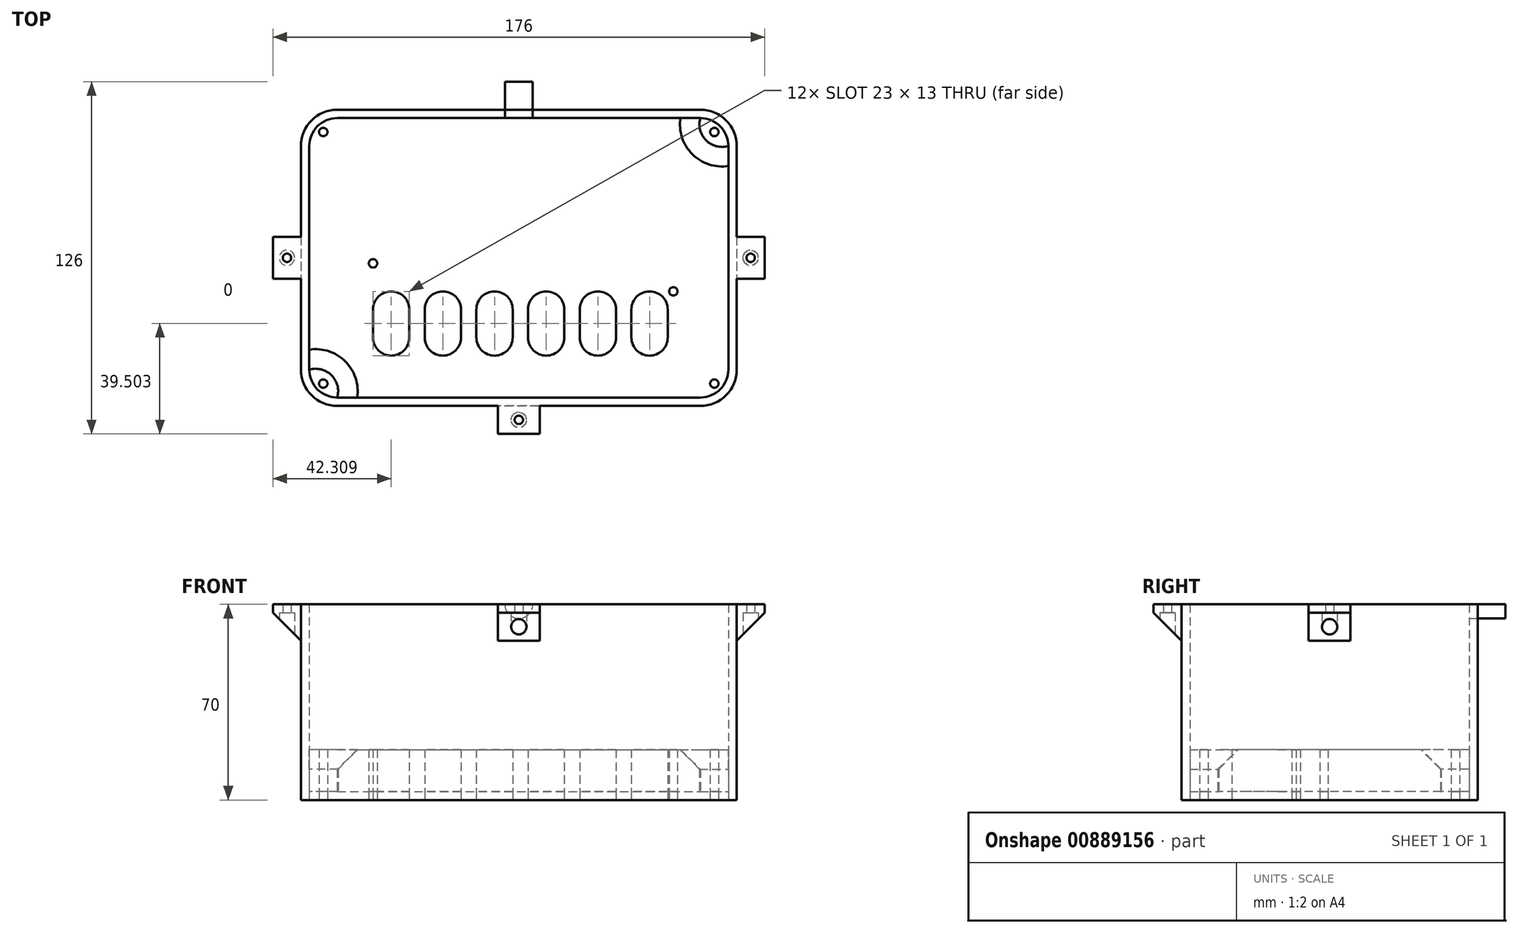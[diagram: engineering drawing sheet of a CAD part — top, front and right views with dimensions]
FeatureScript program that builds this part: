
annotation { "Feature Type Name" : "Feature", "Feature Type Description" : "" }
export const myFeature = defineFeature(function(context is Context, id is Id, definition is map)
    precondition{}
    {
        {
            var Q0;
            Q0=qCreatedBy(makeId("Top.planeOp"),FACE);
            var sketch = newSketch(context, id + "F0", { "sketchPlane" : qUnion([Q0])});
            skLineSegment(sketch, "E0.bottom", {"start": v(-27.14, 18.01) * mm, "end": v(-27.14, 18.01) * mm});
            skLineSegment(sketch, "E0.top", {"start": v(-27.14, -3.99) * mm, "end": v(-27.14, -3.99) * mm});
            skLineSegment(sketch, "E0.left", {"start": v(-33.14, 12.01) * mm, "end": v(-33.14, 2.01) * mm});
            skLineSegment(sketch, "E0.right", {"start": v(-21.14, 12.01) * mm, "end": v(-21.14, 2.01) * mm});
            skPoint(sketch, "E1.visualSharp", {"position": v(-33.14, 18.01) * mm});
            skArc(sketch, "E1.filletArc", {"start": v(-27.14, 18.01) * mm, "mid": v(-31.38, 16.26) * mm, "end": v(-33.14, 12.01) * mm});
            skPoint(sketch, "E2.visualSharp", {"position": v(-21.14, 18.01) * mm});
            skArc(sketch, "E2.filletArc", {"start": v(-21.14, 12.01) * mm, "mid": v(-22.9, 16.26) * mm, "end": v(-27.14, 18.01) * mm});
            skPoint(sketch, "E3.visualSharp", {"position": v(-33.14, -3.99) * mm});
            skArc(sketch, "E3.filletArc", {"start": v(-33.14, 2.01) * mm, "mid": v(-31.38, -2.23) * mm, "end": v(-27.14, -3.99) * mm});
            skArc(sketch, "E4.filletArc", {"start": v(-27.14, -3.99) * mm, "mid": v(-22.9, -2.23) * mm, "end": v(-21.14, 2.01) * mm});
            skArc(sketch, "E5.0", {"start": v(-20.64, 12.01) * mm, "mid": v(-22.49, 16.55) * mm, "end": v(-26.97, 18.51) * mm});
            skArc(sketch, "E5.1", {"start": v(-26.97, -4.49) * mm, "mid": v(-22.49, -2.52) * mm, "end": v(-20.64, 2.01) * mm});
            skArc(sketch, "E5.2", {"start": v(-33.64, 2.01) * mm, "mid": v(-31.68, -2.64) * mm, "end": v(-26.97, -4.49) * mm});
            skLineSegment(sketch, "E5.3", {"start": v(-20.64, 12.01) * mm, "end": v(-20.64, 2.01) * mm});
            skLineSegment(sketch, "E5.4", {"start": v(-33.64, 12.01) * mm, "end": v(-33.64, 2.01) * mm});
            skArc(sketch, "E5.5", {"start": v(-26.97, 18.51) * mm, "mid": v(-31.68, 16.67) * mm, "end": v(-33.64, 12.01) * mm});
            skArc(sketch, "E6.1.0.0", {"start": v(-8.64, 18.01) * mm, "mid": v(-12.88, 16.26) * mm, "end": v(-14.64, 12.01) * mm});
            skArc(sketch, "E6.1.0.1", {"start": v(-8.47, -4.49) * mm, "mid": v(-3.99, -2.52) * mm, "end": v(-2.14, 2.01) * mm});
            skArc(sketch, "E6.1.0.2", {"start": v(-2.14, 12.01) * mm, "mid": v(-3.99, 16.55) * mm, "end": v(-8.47, 18.51) * mm});
            skLineSegment(sketch, "E6.1.0.3", {"start": v(-2.14, 12.01) * mm, "end": v(-2.14, 2.01) * mm});
            skArc(sketch, "E6.1.0.4", {"start": v(-2.64, 12.01) * mm, "mid": v(-4.4, 16.26) * mm, "end": v(-8.64, 18.01) * mm});
            skArc(sketch, "E6.1.0.5", {"start": v(-14.64, 2.01) * mm, "mid": v(-12.88, -2.23) * mm, "end": v(-8.64, -3.99) * mm});
            skArc(sketch, "E6.1.0.6", {"start": v(-8.64, -3.99) * mm, "mid": v(-4.4, -2.23) * mm, "end": v(-2.64, 2.01) * mm});
            skPoint(sketch, "E6.1.0.7", {"position": v(-14.64, -3.99) * mm});
            skPoint(sketch, "E6.1.0.8", {"position": v(-2.64, 18.01) * mm});
            skLineSegment(sketch, "E6.1.0.9", {"start": v(-15.14, 12.01) * mm, "end": v(-15.14, 2.01) * mm});
            skLineSegment(sketch, "E6.1.0.10", {"start": v(-14.64, 12.01) * mm, "end": v(-14.64, 2.01) * mm});
            skArc(sketch, "E6.1.0.11", {"start": v(-8.47, 18.51) * mm, "mid": v(-13.18, 16.67) * mm, "end": v(-15.14, 12.01) * mm});
            skPoint(sketch, "E6.1.0.12", {"position": v(-14.64, 18.01) * mm});
            skLineSegment(sketch, "E6.1.0.13", {"start": v(-2.64, 12.01) * mm, "end": v(-2.64, 2.01) * mm});
            skArc(sketch, "E6.1.0.14", {"start": v(-15.14, 2.01) * mm, "mid": v(-13.18, -2.64) * mm, "end": v(-8.47, -4.49) * mm});
            skArc(sketch, "E6.2.0.0", {"start": v(9.86, 18.01) * mm, "mid": v(5.62, 16.26) * mm, "end": v(3.86, 12.01) * mm});
            skArc(sketch, "E6.2.0.1", {"start": v(10.03, -4.49) * mm, "mid": v(14.51, -2.52) * mm, "end": v(16.36, 2.01) * mm});
            skArc(sketch, "E6.2.0.2", {"start": v(16.36, 12.01) * mm, "mid": v(14.51, 16.55) * mm, "end": v(10.03, 18.51) * mm});
            skLineSegment(sketch, "E6.2.0.3", {"start": v(16.36, 12.01) * mm, "end": v(16.36, 2.01) * mm});
            skArc(sketch, "E6.2.0.4", {"start": v(15.86, 12.01) * mm, "mid": v(14.1, 16.26) * mm, "end": v(9.86, 18.01) * mm});
            skArc(sketch, "E6.2.0.5", {"start": v(3.86, 2.01) * mm, "mid": v(5.62, -2.23) * mm, "end": v(9.86, -3.99) * mm});
            skArc(sketch, "E6.2.0.6", {"start": v(9.86, -3.99) * mm, "mid": v(14.1, -2.23) * mm, "end": v(15.86, 2.01) * mm});
            skPoint(sketch, "E6.2.0.7", {"position": v(3.86, -3.99) * mm});
            skPoint(sketch, "E6.2.0.8", {"position": v(15.86, 18.01) * mm});
            skLineSegment(sketch, "E6.2.0.9", {"start": v(3.36, 12.01) * mm, "end": v(3.36, 2.01) * mm});
            skLineSegment(sketch, "E6.2.0.10", {"start": v(3.86, 12.01) * mm, "end": v(3.86, 2.01) * mm});
            skArc(sketch, "E6.2.0.11", {"start": v(10.03, 18.51) * mm, "mid": v(5.32, 16.67) * mm, "end": v(3.36, 12.01) * mm});
            skPoint(sketch, "E6.2.0.12", {"position": v(3.86, 18.01) * mm});
            skLineSegment(sketch, "E6.2.0.13", {"start": v(15.86, 12.01) * mm, "end": v(15.86, 2.01) * mm});
            skArc(sketch, "E6.2.0.14", {"start": v(3.36, 2.01) * mm, "mid": v(5.32, -2.64) * mm, "end": v(10.03, -4.49) * mm});
            skArc(sketch, "E6.3.0.0", {"start": v(28.36, 18.01) * mm, "mid": v(24.12, 16.26) * mm, "end": v(22.36, 12.01) * mm});
            skArc(sketch, "E6.3.0.1", {"start": v(28.53, -4.49) * mm, "mid": v(33.01, -2.52) * mm, "end": v(34.86, 2.01) * mm});
            skArc(sketch, "E6.3.0.2", {"start": v(34.86, 12.01) * mm, "mid": v(33.01, 16.55) * mm, "end": v(28.53, 18.51) * mm});
            skLineSegment(sketch, "E6.3.0.3", {"start": v(34.86, 12.01) * mm, "end": v(34.86, 2.01) * mm});
            skArc(sketch, "E6.3.0.4", {"start": v(34.36, 12.01) * mm, "mid": v(32.6, 16.26) * mm, "end": v(28.36, 18.01) * mm});
            skArc(sketch, "E6.3.0.5", {"start": v(22.36, 2.01) * mm, "mid": v(24.12, -2.23) * mm, "end": v(28.36, -3.99) * mm});
            skArc(sketch, "E6.3.0.6", {"start": v(28.36, -3.99) * mm, "mid": v(32.6, -2.23) * mm, "end": v(34.36, 2.01) * mm});
            skPoint(sketch, "E6.3.0.7", {"position": v(22.36, -3.99) * mm});
            skPoint(sketch, "E6.3.0.8", {"position": v(34.36, 18.01) * mm});
            skLineSegment(sketch, "E6.3.0.9", {"start": v(21.86, 12.01) * mm, "end": v(21.86, 2.01) * mm});
            skLineSegment(sketch, "E6.3.0.10", {"start": v(22.36, 12.01) * mm, "end": v(22.36, 2.01) * mm});
            skArc(sketch, "E6.3.0.11", {"start": v(28.53, 18.51) * mm, "mid": v(23.82, 16.67) * mm, "end": v(21.86, 12.01) * mm});
            skPoint(sketch, "E6.3.0.12", {"position": v(22.36, 18.01) * mm});
            skLineSegment(sketch, "E6.3.0.13", {"start": v(34.36, 12.01) * mm, "end": v(34.36, 2.01) * mm});
            skArc(sketch, "E6.3.0.14", {"start": v(21.86, 2.01) * mm, "mid": v(23.82, -2.64) * mm, "end": v(28.53, -4.49) * mm});
            skArc(sketch, "E6.4.0.0", {"start": v(46.86, 18.01) * mm, "mid": v(42.62, 16.26) * mm, "end": v(40.86, 12.01) * mm});
            skArc(sketch, "E6.4.0.1", {"start": v(47.03, -4.49) * mm, "mid": v(51.51, -2.52) * mm, "end": v(53.36, 2.01) * mm});
            skArc(sketch, "E6.4.0.2", {"start": v(53.36, 12.01) * mm, "mid": v(51.51, 16.55) * mm, "end": v(47.03, 18.51) * mm});
            skLineSegment(sketch, "E6.4.0.3", {"start": v(53.36, 12.01) * mm, "end": v(53.36, 2.01) * mm});
            skArc(sketch, "E6.4.0.4", {"start": v(52.86, 12.01) * mm, "mid": v(51.1, 16.26) * mm, "end": v(46.86, 18.01) * mm});
            skArc(sketch, "E6.4.0.5", {"start": v(40.86, 2.01) * mm, "mid": v(42.62, -2.23) * mm, "end": v(46.86, -3.99) * mm});
            skArc(sketch, "E6.4.0.6", {"start": v(46.86, -3.99) * mm, "mid": v(51.1, -2.23) * mm, "end": v(52.86, 2.01) * mm});
            skPoint(sketch, "E6.4.0.7", {"position": v(40.86, -3.99) * mm});
            skPoint(sketch, "E6.4.0.8", {"position": v(52.86, 18.01) * mm});
            skLineSegment(sketch, "E6.4.0.9", {"start": v(40.36, 12.01) * mm, "end": v(40.36, 2.01) * mm});
            skLineSegment(sketch, "E6.4.0.10", {"start": v(40.86, 12.01) * mm, "end": v(40.86, 2.01) * mm});
            skArc(sketch, "E6.4.0.11", {"start": v(47.03, 18.51) * mm, "mid": v(42.32, 16.67) * mm, "end": v(40.36, 12.01) * mm});
            skPoint(sketch, "E6.4.0.12", {"position": v(40.86, 18.01) * mm});
            skLineSegment(sketch, "E6.4.0.13", {"start": v(52.86, 12.01) * mm, "end": v(52.86, 2.01) * mm});
            skArc(sketch, "E6.4.0.14", {"start": v(40.36, 2.01) * mm, "mid": v(42.32, -2.64) * mm, "end": v(47.03, -4.49) * mm});
            skArc(sketch, "E6.5.0.0", {"start": v(65.36, 18.01) * mm, "mid": v(61.12, 16.26) * mm, "end": v(59.36, 12.01) * mm});
            skArc(sketch, "E6.5.0.1", {"start": v(65.53, -4.49) * mm, "mid": v(70.01, -2.52) * mm, "end": v(71.86, 2.01) * mm});
            skArc(sketch, "E6.5.0.2", {"start": v(71.86, 12.01) * mm, "mid": v(70.01, 16.55) * mm, "end": v(65.53, 18.51) * mm});
            skLineSegment(sketch, "E6.5.0.3", {"start": v(71.86, 12.01) * mm, "end": v(71.86, 2.01) * mm});
            skArc(sketch, "E6.5.0.4", {"start": v(71.36, 12.01) * mm, "mid": v(69.6, 16.26) * mm, "end": v(65.36, 18.01) * mm});
            skArc(sketch, "E6.5.0.5", {"start": v(59.36, 2.01) * mm, "mid": v(61.12, -2.23) * mm, "end": v(65.36, -3.99) * mm});
            skArc(sketch, "E6.5.0.6", {"start": v(65.36, -3.99) * mm, "mid": v(69.6, -2.23) * mm, "end": v(71.36, 2.01) * mm});
            skPoint(sketch, "E6.5.0.7", {"position": v(59.36, -3.99) * mm});
            skPoint(sketch, "E6.5.0.8", {"position": v(71.36, 18.01) * mm});
            skLineSegment(sketch, "E6.5.0.9", {"start": v(58.86, 12.01) * mm, "end": v(58.86, 2.01) * mm});
            skLineSegment(sketch, "E6.5.0.10", {"start": v(59.36, 12.01) * mm, "end": v(59.36, 2.01) * mm});
            skArc(sketch, "E6.5.0.11", {"start": v(65.53, 18.51) * mm, "mid": v(60.82, 16.67) * mm, "end": v(58.86, 12.01) * mm});
            skPoint(sketch, "E6.5.0.12", {"position": v(59.36, 18.01) * mm});
            skLineSegment(sketch, "E6.5.0.13", {"start": v(71.36, 12.01) * mm, "end": v(71.36, 2.01) * mm});
            skArc(sketch, "E6.5.0.14", {"start": v(58.86, 2.01) * mm, "mid": v(60.82, -2.64) * mm, "end": v(65.53, -4.49) * mm});
            skLineSegment(sketch, "E6.direction1", {"start": v(-33.14, -3.99) * mm, "end": v(-14.64, -3.99) * mm, "construction": true});
            skLineSegment(sketch, "E7", {"start": v(-21.14, 12.01) * mm, "end": v(-14.64, 12.01) * mm});
            skPoint(sketch, "E8", {"position": v(71.86, 18.51) * mm});
            skLineSegment(sketch, "E9", {"start": v(-8.47, 18.51) * mm, "end": v(-37.8, 18.51) * mm, "construction": true});
            skLineSegment(sketch, "E10.trimOffspring", {"start": v(-33.64, 18.51) * mm, "end": v(-33.64, 28.51) * mm, "construction": true});
            skLineSegment(sketch, "E11.bottom", {"start": v(-46.45, 80.51) * mm, "end": v(83.55, 80.51) * mm});
            skLineSegment(sketch, "E11.top", {"start": v(-46.45, -19.49) * mm, "end": v(83.55, -19.49) * mm});
            skLineSegment(sketch, "E11.left", {"start": v(-56.45, 70.51) * mm, "end": v(-56.45, -9.49) * mm});
            skLineSegment(sketch, "E11.right", {"start": v(93.55, 70.51) * mm, "end": v(93.55, -9.49) * mm});
            skLineSegment(sketch, "E12", {"start": v(-56.45, 80.51) * mm, "end": v(93.55, -19.49) * mm, "construction": true});
            skLineSegment(sketch, "E13", {"start": v(93.55, 80.51) * mm, "end": v(-56.45, -19.49) * mm, "construction": true});
            skLineSegment(sketch, "E14", {"start": v(18.55, -19.49) * mm, "end": v(18.55, 80.51) * mm, "construction": true});
            skLineSegment(sketch, "E15", {"start": v(10.03, -4.49) * mm, "end": v(10.03, -19.49) * mm, "construction": true});
            skPoint(sketch, "E16.visualSharp", {"position": v(93.55, 80.51) * mm});
            skArc(sketch, "E16.filletArc", {"start": v(93.55, 70.51) * mm, "mid": v(90.62, 77.59) * mm, "end": v(83.55, 80.51) * mm});
            skPoint(sketch, "E17.visualSharp", {"position": v(-56.45, 80.51) * mm});
            skArc(sketch, "E17.filletArc", {"start": v(-46.45, 80.51) * mm, "mid": v(-53.52, 77.59) * mm, "end": v(-56.45, 70.51) * mm});
            skPoint(sketch, "E18.visualSharp", {"position": v(-56.45, -19.49) * mm});
            skArc(sketch, "E18.filletArc", {"start": v(-56.45, -9.49) * mm, "mid": v(-53.52, -16.56) * mm, "end": v(-46.45, -19.49) * mm});
            skPoint(sketch, "E19.visualSharp", {"position": v(93.55, -19.49) * mm});
            skArc(sketch, "E19.filletArc", {"start": v(83.55, -19.49) * mm, "mid": v(90.62, -16.56) * mm, "end": v(93.55, -9.49) * mm});
            skArc(sketch, "E20.0", {"start": v(-59.45, -9.49) * mm, "mid": v(-55.64, -18.68) * mm, "end": v(-46.45, -22.49) * mm});
            skLineSegment(sketch, "E20.1", {"start": v(-59.45, 70.51) * mm, "end": v(-59.45, -9.49) * mm});
            skLineSegment(sketch, "E20.2", {"start": v(-46.45, -22.49) * mm, "end": v(83.55, -22.49) * mm});
            skArc(sketch, "E20.3", {"start": v(-46.45, 83.51) * mm, "mid": v(-55.64, 79.7) * mm, "end": v(-59.45, 70.51) * mm});
            skArc(sketch, "E20.4", {"start": v(83.55, -22.49) * mm, "mid": v(92.74, -18.68) * mm, "end": v(96.55, -9.49) * mm});
            skLineSegment(sketch, "E20.5", {"start": v(96.55, 70.51) * mm, "end": v(96.55, -9.49) * mm});
            skArc(sketch, "E20.6", {"start": v(96.55, 70.51) * mm, "mid": v(92.74, 79.7) * mm, "end": v(83.55, 83.51) * mm});
            skLineSegment(sketch, "E20.7", {"start": v(-46.45, 83.51) * mm, "end": v(83.55, 83.51) * mm});
            skLineSegment(sketch, "E21", {"start": v(71.86, 2.01) * mm, "end": v(71.86, 18.51) * mm, "construction": true});
            skLineSegment(sketch, "E22", {"start": v(28.53, 18.51) * mm, "end": v(65.53, 18.51) * mm, "construction": true});
            skLineSegment(sketch, "E23.trimOffspring", {"start": v(71.86, 18.51) * mm, "end": v(73.86, 18.51) * mm, "construction": true});
            skPoint(sketch, "E24", {"position": v(-33.64, 28.51) * mm});
            skLineSegment(sketch, "E25", {"start": v(93.55, -9.49) * mm, "end": v(83.55, -19.49) * mm, "construction": true});
            skPoint(sketch, "E26", {"position": v(88.55, -14.49) * mm});
            skLineSegment(sketch, "E27", {"start": v(-46.45, -19.49) * mm, "end": v(-56.45, -9.49) * mm, "construction": true});
            skLineSegment(sketch, "E28", {"start": v(-56.45, 70.51) * mm, "end": v(-46.45, 80.51) * mm, "construction": true});
            skLineSegment(sketch, "E29", {"start": v(93.55, 70.51) * mm, "end": v(83.55, 80.51) * mm, "construction": true});
            skPoint(sketch, "E30", {"position": v(-51.45, -14.49) * mm});
            skPoint(sketch, "E31", {"position": v(-51.45, 75.51) * mm});
            skPoint(sketch, "E32", {"position": v(88.55, 75.51) * mm});
            skSolve(sketch);
        }
        {
            var Q0;
            Q0=makeQuery(id+"F0.imprint","IMPRINT",FACE,{"disambiguationData":[TD([[makeQuery(id+"F0.imprint","IMPRINT",EDGE,{"derivedFrom":sQuery(id+"F0.wireOp",EDGE,"E5.0")}),-1.0]])]});
            extrude(context, id + "F1", {"entities" : qUnion([Q0]), "depth" : 3 * mm, "offsetDistance" : 25 * mm});
        }
        {
            var Q0;
            Q0=makeQuery(id+"F0.imprint","IMPRINT",FACE,{"disambiguationData":[TD([[makeQuery(id+"F0.imprint","IMPRINT",EDGE,{"derivedFrom":sQuery(id+"F0.wireOp",EDGE,"E11.bottom")}),1.0]])]});
            extrude(context, id + "F2", {"entities" : qUnion([Q0]), "depth" : 70 * mm, "offsetDistance" : 25 * mm});
        }
        {
            var Q0;
            Q0=makeQuery(id+"F2.opExtrude","SWEPT_FACE",FACE,{"disambiguationData":[OSD([sQuery(id+"F0.wireOp",EDGE,"E20.7")])]});
            var sketch = newSketch(context, id + "F3", { "sketchPlane" : qUnion([Q0])});
            skLineSegment(sketch, "E33", {"start": v(-83.55, 70) * mm, "end": v(46.45, 70) * mm, "construction": true});
            skPoint(sketch, "E34", {"position": v(-18.55, 70) * mm});
            skArc(sketch, "E35", {"start": v(-13.55, 70) * mm, "mid": v(-18.55, 65) * mm, "end": v(-23.55, 70) * mm});
            skArc(sketch, "E36.0", {"start": v(-11.55, 70) * mm, "mid": v(-18.55, 63) * mm, "end": v(-25.55, 70) * mm});
            skSolve(sketch);
        }
        {
            var Q0;
            Q0=sQuery(id+"F3.wireOp",VERTEX,"E34");
            var Q1;
            Q1=makeQuery(id+"F2.opExtrude","SWEPT_BODY",BODY,{"disambiguationData":[OSD([sQuery(id+"F0.wireOp",EDGE,"E11.bottom"),sQuery(id+"F0.wireOp",EDGE,"E11.top"),sQuery(id+"F0.wireOp",EDGE,"E11.left"),sQuery(id+"F0.wireOp",EDGE,"E11.right"),sQuery(id+"F0.wireOp",EDGE,"E16.filletArc"),sQuery(id+"F0.wireOp",EDGE,"E17.filletArc"),sQuery(id+"F0.wireOp",EDGE,"E18.filletArc"),sQuery(id+"F0.wireOp",EDGE,"E19.filletArc"),sQuery(id+"F0.wireOp",EDGE,"E20.0"),sQuery(id+"F0.wireOp",EDGE,"E20.1"),sQuery(id+"F0.wireOp",EDGE,"E20.2"),sQuery(id+"F0.wireOp",EDGE,"E20.3"),sQuery(id+"F0.wireOp",EDGE,"E20.4"),sQuery(id+"F0.wireOp",EDGE,"E20.5"),sQuery(id+"F0.wireOp",EDGE,"E20.6"),sQuery(id+"F0.wireOp",EDGE,"E20.7")])]});
            hole(context, id + "F4", {"style" : HoleStyle.SIMPLE, "endStyle" : HoleEndStyle.BLIND, "holeDiameter" : 10 * mm, "majorDiameter" : 5 * mm, "holeDepth" : 5 * mm, "isTappedThrough" : true, "tappedDepth" : 12 * mm, "tapClearance" : 3, "locations" : qUnion([Q0]), "scope" : qUnion([Q1])});
        }
        {
            var Q0;
            {var subQ0=sQuery(id+"F3.wireOp",EDGE,"E35");Q0=makeQuery(id+"F3.imprint","IMPRINT",FACE,{"disambiguationData":[TD([[makeQuery(id+"F3.imprint","IMPRINT",EDGE,{"derivedFrom":subQ0}),1.0]])]});}
            extrude(context, id + "F5", {"entities" : qUnion([Q0]), "operationType" : NewBodyOperationType.ADD, "depth" : 10 * mm, "offsetDistance" : 25 * mm});
        }
        {
            var Q0;
            {var subQ0=sQuery(id+"F3.wireOp",EDGE,"E35");var subQ1=sQuery(id+"F0.wireOp",EDGE,"E20.7");var subQ2=makeQuery(id+"F2.opExtrude","CAP_EDGE",EDGE,{"disambiguationData":[OSD([subQ1])],"isStart":false});Q0=makeQuery(id+"F5.boolean.opBoolean","MERGE",FACE,{"derivedFrom":[makeQuery(id+"F2.opExtrude","CAP_FACE",FACE,{"disambiguationData":[OSD([sQuery(id+"F0.wireOp",EDGE,"E11.bottom"),sQuery(id+"F0.wireOp",EDGE,"E11.top"),sQuery(id+"F0.wireOp",EDGE,"E11.left"),sQuery(id+"F0.wireOp",EDGE,"E11.right"),sQuery(id+"F0.wireOp",EDGE,"E16.filletArc"),sQuery(id+"F0.wireOp",EDGE,"E17.filletArc"),sQuery(id+"F0.wireOp",EDGE,"E18.filletArc"),sQuery(id+"F0.wireOp",EDGE,"E19.filletArc"),sQuery(id+"F0.wireOp",EDGE,"E20.0"),sQuery(id+"F0.wireOp",EDGE,"E20.1"),sQuery(id+"F0.wireOp",EDGE,"E20.2"),sQuery(id+"F0.wireOp",EDGE,"E20.3"),sQuery(id+"F0.wireOp",EDGE,"E20.4"),sQuery(id+"F0.wireOp",EDGE,"E20.5"),sQuery(id+"F0.wireOp",EDGE,"E20.6"),subQ1])],"isStart":false}),makeQuery(id+"F5.opExtrude","SWEPT_FACE",FACE,{"disambiguationData":[OSD([subQ1]),TDD([makeQuery(id+"F3.imprint","IMPRINT",EDGE,{"disambiguationData":[TD([[makeQuery(id+"F3.imprint","INTERSECT",VERTEX,{"disambiguationData":[OD(0.0)],"derivedFrom":[subQ2,subQ0]}),1.0]])],"derivedFrom":subQ2})])]}),makeQuery(id+"F5.opExtrude","SWEPT_FACE",FACE,{"disambiguationData":[OSD([subQ1]),TDD([makeQuery(id+"F3.imprint","IMPRINT",EDGE,{"disambiguationData":[TD([[makeQuery(id+"F3.imprint","INTERSECT",VERTEX,{"disambiguationData":[OD(1.0)],"derivedFrom":[subQ2,subQ0]}),-1.0]])],"derivedFrom":subQ2})])]})]});}
            var sketch = newSketch(context, id + "F6", { "sketchPlane" : qUnion([Q0])});
            skPoint(sketch, "E37.middle", {"position": v(-59.45, 30.51) * mm});
            skLineSegment(sketch, "E38.bottom", {"start": v(-59.45, 23.01) * mm, "end": v(-69.45, 23.01) * mm});
            skLineSegment(sketch, "E38.top", {"start": v(-59.45, 38.01) * mm, "end": v(-69.45, 38.01) * mm});
            skLineSegment(sketch, "E38.left", {"start": v(-59.45, 23.01) * mm, "end": v(-59.45, 38.01) * mm});
            skLineSegment(sketch, "E38.right", {"start": v(-69.45, 23.01) * mm, "end": v(-69.45, 38.01) * mm});
            skLineSegment(sketch, "E39", {"start": v(18.55, -22.49) * mm, "end": v(18.55, 80.54) * mm, "construction": true});
            skPoint(sketch, "E40.MirrorP", {"position": v(96.55, 30.51) * mm});
            skLineSegment(sketch, "E41.MirrorCS", {"start": v(96.55, 38.01) * mm, "end": v(106.55, 38.01) * mm});
            skLineSegment(sketch, "E42.MirrorCS", {"start": v(106.55, 23.01) * mm, "end": v(106.55, 38.01) * mm});
            skLineSegment(sketch, "E43.MirrorCS", {"start": v(96.55, 23.01) * mm, "end": v(106.55, 23.01) * mm});
            skLineSegment(sketch, "E44.MirrorCS", {"start": v(96.55, 23.01) * mm, "end": v(96.55, 38.01) * mm});
            skPoint(sketch, "E45.MirrorP", {"position": v(101.55, 30.51) * mm});
            skLineSegment(sketch, "E46.bottom", {"start": v(11.05, -22.49) * mm, "end": v(26.05, -22.49) * mm});
            skLineSegment(sketch, "E46.top", {"start": v(11.05, -32.49) * mm, "end": v(26.05, -32.49) * mm});
            skLineSegment(sketch, "E46.left", {"start": v(11.05, -22.49) * mm, "end": v(11.05, -32.49) * mm});
            skLineSegment(sketch, "E46.right", {"start": v(26.05, -22.49) * mm, "end": v(26.05, -32.49) * mm});
            skLineSegment(sketch, "E47", {"start": v(11.05, -22.49) * mm, "end": v(26.05, -32.49) * mm, "construction": true});
            skLineSegment(sketch, "E48", {"start": v(26.05, -22.49) * mm, "end": v(11.05, -32.49) * mm, "construction": true});
            skPoint(sketch, "E49", {"position": v(18.55, -27.49) * mm});
            skSolve(sketch);
        }
        {
            var Q0;
            Q0=makeQuery(id+"F6.imprint","IMPRINT",FACE,{"disambiguationData":[TD([[makeQuery(id+"F6.imprint","IMPRINT",EDGE,{"derivedFrom":sQuery(id+"F6.wireOp",EDGE,"E38.bottom")}),-1.0]])]});
            var Q1;
            Q1=makeQuery(id+"F6.imprint","IMPRINT",FACE,{"disambiguationData":[TD([[makeQuery(id+"F6.imprint","IMPRINT",EDGE,{"derivedFrom":sQuery(id+"F6.wireOp",EDGE,"E41.MirrorCS")}),-1.0]])]});
            var Q2;
            Q2=makeQuery(id+"F6.imprint","IMPRINT",FACE,{"disambiguationData":[TD([[makeQuery(id+"F6.imprint","IMPRINT",EDGE,{"derivedFrom":sQuery(id+"F6.wireOp",EDGE,"E46.bottom")}),-1.0]])]});
            extrude(context, id + "F7", {"entities" : qUnion([Q0, Q1, Q2]), "operationType" : NewBodyOperationType.ADD, "depth" : -15 * mm, "offsetDistance" : 25 * mm});
        }
        {
            var Q0;
            Q0=makeQuery(id+"F7.opExtrude","CAP_FACE",FACE,{"disambiguationData":[OSD([sQuery(id+"F6.wireOp",EDGE,"E38.bottom"),sQuery(id+"F6.wireOp",EDGE,"E38.top"),sQuery(id+"F6.wireOp",EDGE,"E38.left"),sQuery(id+"F6.wireOp",EDGE,"E38.right")])],"isStart":false});
            var sketch = newSketch(context, id + "F8", { "sketchPlane" : qUnion([Q0])});
            skLineSegment(sketch, "E50", {"start": v(-69.45, -23.01) * mm, "end": v(-59.45, -38.01) * mm, "construction": true});
            skLineSegment(sketch, "E51", {"start": v(-69.45, -38.01) * mm, "end": v(-59.45, -23.01) * mm, "construction": true});
            skPoint(sketch, "E52", {"position": v(-64.45, -30.51) * mm});
            skLineSegment(sketch, "E53", {"start": v(-59.45, -23.01) * mm, "end": v(96.55, -23.01) * mm, "construction": true});
            skLineSegment(sketch, "E54", {"start": v(18.55, -23.01) * mm, "end": v(18.55, 11.18) * mm});
            skPoint(sketch, "E55.MirrorP", {"position": v(101.55, -30.51) * mm});
            skSolve(sketch);
        }
        {
            var Q0;
            Q0=sQuery(id+"F8.wireOp",VERTEX,"E55.MirrorP");
            var Q1;
            Q1=sQuery(id+"F8.wireOp",VERTEX,"E52");
            var Q2;
            Q2=makeQuery(id+"F2.opExtrude","SWEPT_BODY",BODY,{"disambiguationData":[OSD([sQuery(id+"F0.wireOp",EDGE,"E11.bottom"),sQuery(id+"F0.wireOp",EDGE,"E11.top"),sQuery(id+"F0.wireOp",EDGE,"E11.left"),sQuery(id+"F0.wireOp",EDGE,"E11.right"),sQuery(id+"F0.wireOp",EDGE,"E16.filletArc"),sQuery(id+"F0.wireOp",EDGE,"E17.filletArc"),sQuery(id+"F0.wireOp",EDGE,"E18.filletArc"),sQuery(id+"F0.wireOp",EDGE,"E19.filletArc"),sQuery(id+"F0.wireOp",EDGE,"E20.0"),sQuery(id+"F0.wireOp",EDGE,"E20.1"),sQuery(id+"F0.wireOp",EDGE,"E20.2"),sQuery(id+"F0.wireOp",EDGE,"E20.3"),sQuery(id+"F0.wireOp",EDGE,"E20.4"),sQuery(id+"F0.wireOp",EDGE,"E20.5"),sQuery(id+"F0.wireOp",EDGE,"E20.6"),sQuery(id+"F0.wireOp",EDGE,"E20.7")])]});
            hole(context, id + "F9", {"style" : HoleStyle.C_BORE, "endStyle" : HoleEndStyle.BLIND, "holeDiameter" : 3 * mm, "cBoreDiameter" : 5.5 * mm, "cBoreDepth" : 12 * mm, "majorDiameter" : 5 * mm, "holeDepth" : 15 * mm, "isTappedThrough" : true, "tappedDepth" : 12 * mm, "tapClearance" : 3, "locations" : qUnion([Q0, Q1]), "scope" : qUnion([Q2])});
        }
        {
            var Q0;
            Q0=makeQuery(id+"F7.opExtrude","CAP_EDGE",EDGE,{"disambiguationData":[OSD([sQuery(id+"F6.wireOp",EDGE,"E38.right")])],"isStart":false});
            var Q1;
            Q1=makeQuery(id+"F7.opExtrude","CAP_EDGE",EDGE,{"disambiguationData":[OSD([sQuery(id+"F6.wireOp",EDGE,"E42.MirrorCS")])],"isStart":false});
            chamfer(context, id + "F10", {"entities" : qUnion([Q0, Q1]), "width" : 12 * mm, "tangentPropagation" : true});
        }
        {
            var Q0;
            Q0=sQuery(id+"F0.wireOp",VERTEX,"E24");
            var Q1;
            Q1=sQuery(id+"F0.wireOp",VERTEX,"E23.trimOffspring.end");
            var Q2;
            Q2=makeQuery(id+"F1.opExtrude","SWEPT_BODY",BODY,{"disambiguationData":[OSD([sQuery(id+"F0.wireOp",EDGE,"E5.0"),sQuery(id+"F0.wireOp",EDGE,"E5.1"),sQuery(id+"F0.wireOp",EDGE,"E5.2"),sQuery(id+"F0.wireOp",EDGE,"E5.3"),sQuery(id+"F0.wireOp",EDGE,"E5.4"),sQuery(id+"F0.wireOp",EDGE,"E5.5"),sQuery(id+"F0.wireOp",EDGE,"E6.1.0.1"),sQuery(id+"F0.wireOp",EDGE,"E6.1.0.2"),sQuery(id+"F0.wireOp",EDGE,"E6.1.0.3"),sQuery(id+"F0.wireOp",EDGE,"E6.1.0.9"),sQuery(id+"F0.wireOp",EDGE,"E6.1.0.11"),sQuery(id+"F0.wireOp",EDGE,"E6.1.0.14"),sQuery(id+"F0.wireOp",EDGE,"E6.2.0.1"),sQuery(id+"F0.wireOp",EDGE,"E6.2.0.2"),sQuery(id+"F0.wireOp",EDGE,"E6.2.0.3"),sQuery(id+"F0.wireOp",EDGE,"E6.2.0.9"),sQuery(id+"F0.wireOp",EDGE,"E6.2.0.11"),sQuery(id+"F0.wireOp",EDGE,"E6.2.0.14"),sQuery(id+"F0.wireOp",EDGE,"E6.3.0.1"),sQuery(id+"F0.wireOp",EDGE,"E6.3.0.2"),sQuery(id+"F0.wireOp",EDGE,"E6.3.0.3"),sQuery(id+"F0.wireOp",EDGE,"E6.3.0.9"),sQuery(id+"F0.wireOp",EDGE,"E6.3.0.11"),sQuery(id+"F0.wireOp",EDGE,"E6.3.0.14"),sQuery(id+"F0.wireOp",EDGE,"E6.4.0.1"),sQuery(id+"F0.wireOp",EDGE,"E6.4.0.2"),sQuery(id+"F0.wireOp",EDGE,"E6.4.0.3"),sQuery(id+"F0.wireOp",EDGE,"E6.4.0.9"),sQuery(id+"F0.wireOp",EDGE,"E6.4.0.11"),sQuery(id+"F0.wireOp",EDGE,"E6.4.0.14"),sQuery(id+"F0.wireOp",EDGE,"E6.5.0.1"),sQuery(id+"F0.wireOp",EDGE,"E6.5.0.2"),sQuery(id+"F0.wireOp",EDGE,"E6.5.0.3"),sQuery(id+"F0.wireOp",EDGE,"E6.5.0.9"),sQuery(id+"F0.wireOp",EDGE,"E6.5.0.11"),sQuery(id+"F0.wireOp",EDGE,"E6.5.0.14"),sQuery(id+"F0.wireOp",EDGE,"E11.bottom"),sQuery(id+"F0.wireOp",EDGE,"E11.top"),sQuery(id+"F0.wireOp",EDGE,"E11.left"),sQuery(id+"F0.wireOp",EDGE,"E11.right"),sQuery(id+"F0.wireOp",EDGE,"E16.filletArc"),sQuery(id+"F0.wireOp",EDGE,"E17.filletArc"),sQuery(id+"F0.wireOp",EDGE,"E18.filletArc"),sQuery(id+"F0.wireOp",EDGE,"E19.filletArc")])]});
            hole(context, id + "F11", {"style" : HoleStyle.SIMPLE, "endStyle" : HoleEndStyle.BLIND, "oppositeDirection" : true, "holeDiameter" : 3 * mm, "majorDiameter" : 5 * mm, "holeDepth" : 5 * mm, "isTappedThrough" : true, "tappedDepth" : 12 * mm, "tapClearance" : 3, "locations" : qUnion([Q0, Q1]), "scope" : qUnion([Q2])});
        }
        {
            var Q0;
            Q0=sQuery(id+"F0.wireOp",VERTEX,"E32");
            var Q1;
            Q1=sQuery(id+"F0.wireOp",VERTEX,"E31");
            var Q2;
            Q2=sQuery(id+"F0.wireOp",VERTEX,"E30");
            var Q3;
            Q3=sQuery(id+"F0.wireOp",VERTEX,"E26");
            var Q4;
            Q4=makeQuery(id+"F1.opExtrude","SWEPT_BODY",BODY,{"disambiguationData":[OSD([sQuery(id+"F0.wireOp",EDGE,"E5.0"),sQuery(id+"F0.wireOp",EDGE,"E5.1"),sQuery(id+"F0.wireOp",EDGE,"E5.2"),sQuery(id+"F0.wireOp",EDGE,"E5.3"),sQuery(id+"F0.wireOp",EDGE,"E5.4"),sQuery(id+"F0.wireOp",EDGE,"E5.5"),sQuery(id+"F0.wireOp",EDGE,"E6.1.0.1"),sQuery(id+"F0.wireOp",EDGE,"E6.1.0.2"),sQuery(id+"F0.wireOp",EDGE,"E6.1.0.3"),sQuery(id+"F0.wireOp",EDGE,"E6.1.0.9"),sQuery(id+"F0.wireOp",EDGE,"E6.1.0.11"),sQuery(id+"F0.wireOp",EDGE,"E6.1.0.14"),sQuery(id+"F0.wireOp",EDGE,"E6.2.0.1"),sQuery(id+"F0.wireOp",EDGE,"E6.2.0.2"),sQuery(id+"F0.wireOp",EDGE,"E6.2.0.3"),sQuery(id+"F0.wireOp",EDGE,"E6.2.0.9"),sQuery(id+"F0.wireOp",EDGE,"E6.2.0.11"),sQuery(id+"F0.wireOp",EDGE,"E6.2.0.14"),sQuery(id+"F0.wireOp",EDGE,"E6.3.0.1"),sQuery(id+"F0.wireOp",EDGE,"E6.3.0.2"),sQuery(id+"F0.wireOp",EDGE,"E6.3.0.3"),sQuery(id+"F0.wireOp",EDGE,"E6.3.0.9"),sQuery(id+"F0.wireOp",EDGE,"E6.3.0.11"),sQuery(id+"F0.wireOp",EDGE,"E6.3.0.14"),sQuery(id+"F0.wireOp",EDGE,"E6.4.0.1"),sQuery(id+"F0.wireOp",EDGE,"E6.4.0.2"),sQuery(id+"F0.wireOp",EDGE,"E6.4.0.3"),sQuery(id+"F0.wireOp",EDGE,"E6.4.0.9"),sQuery(id+"F0.wireOp",EDGE,"E6.4.0.11"),sQuery(id+"F0.wireOp",EDGE,"E6.4.0.14"),sQuery(id+"F0.wireOp",EDGE,"E6.5.0.1"),sQuery(id+"F0.wireOp",EDGE,"E6.5.0.2"),sQuery(id+"F0.wireOp",EDGE,"E6.5.0.3"),sQuery(id+"F0.wireOp",EDGE,"E6.5.0.9"),sQuery(id+"F0.wireOp",EDGE,"E6.5.0.11"),sQuery(id+"F0.wireOp",EDGE,"E6.5.0.14"),sQuery(id+"F0.wireOp",EDGE,"E11.bottom"),sQuery(id+"F0.wireOp",EDGE,"E11.top"),sQuery(id+"F0.wireOp",EDGE,"E11.left"),sQuery(id+"F0.wireOp",EDGE,"E11.right"),sQuery(id+"F0.wireOp",EDGE,"E16.filletArc"),sQuery(id+"F0.wireOp",EDGE,"E17.filletArc"),sQuery(id+"F0.wireOp",EDGE,"E18.filletArc"),sQuery(id+"F0.wireOp",EDGE,"E19.filletArc")])]});
            hole(context, id + "F12", {"style" : HoleStyle.SIMPLE, "endStyle" : HoleEndStyle.BLIND, "oppositeDirection" : true, "holeDiameter" : 3 * mm, "majorDiameter" : 5 * mm, "holeDepth" : 5 * mm, "isTappedThrough" : true, "tappedDepth" : 12 * mm, "tapClearance" : 3, "locations" : qUnion([Q0, Q1, Q2, Q3]), "scope" : qUnion([Q4])});
        }
        {
            var Q0;
            Q0=makeQuery(id+"F7.opExtrude","CAP_FACE",FACE,{"disambiguationData":[OSD([sQuery(id+"F6.wireOp",EDGE,"E46.bottom"),sQuery(id+"F6.wireOp",EDGE,"E46.top"),sQuery(id+"F6.wireOp",EDGE,"E46.left"),sQuery(id+"F6.wireOp",EDGE,"E46.right")])],"isStart":false});
            var sketch = newSketch(context, id + "F13", { "sketchPlane" : qUnion([Q0])});
            skLineSegment(sketch, "E56", {"start": v(26.05, 22.49) * mm, "end": v(11.05, 32.49) * mm, "construction": true});
            skLineSegment(sketch, "E57", {"start": v(11.05, 22.49) * mm, "end": v(26.05, 32.49) * mm, "construction": true});
            skPoint(sketch, "E58", {"position": v(18.55, 27.49) * mm});
            skSolve(sketch);
        }
        {
            var Q0;
            Q0=sQuery(id+"F13.wireOp",VERTEX,"E58");
            var Q1;
            Q1=makeQuery(id+"F2.opExtrude","SWEPT_BODY",BODY,{"disambiguationData":[OSD([sQuery(id+"F0.wireOp",EDGE,"E11.bottom"),sQuery(id+"F0.wireOp",EDGE,"E11.top"),sQuery(id+"F0.wireOp",EDGE,"E11.left"),sQuery(id+"F0.wireOp",EDGE,"E11.right"),sQuery(id+"F0.wireOp",EDGE,"E16.filletArc"),sQuery(id+"F0.wireOp",EDGE,"E17.filletArc"),sQuery(id+"F0.wireOp",EDGE,"E18.filletArc"),sQuery(id+"F0.wireOp",EDGE,"E19.filletArc"),sQuery(id+"F0.wireOp",EDGE,"E20.0"),sQuery(id+"F0.wireOp",EDGE,"E20.1"),sQuery(id+"F0.wireOp",EDGE,"E20.2"),sQuery(id+"F0.wireOp",EDGE,"E20.3"),sQuery(id+"F0.wireOp",EDGE,"E20.4"),sQuery(id+"F0.wireOp",EDGE,"E20.5"),sQuery(id+"F0.wireOp",EDGE,"E20.6"),sQuery(id+"F0.wireOp",EDGE,"E20.7")])]});
            hole(context, id + "F14", {"style" : HoleStyle.C_BORE, "endStyle" : HoleEndStyle.BLIND, "holeDiameter" : 3 * mm, "cBoreDiameter" : 5.5 * mm, "cBoreDepth" : 12 * mm, "majorDiameter" : 5 * mm, "holeDepth" : 15 * mm, "isTappedThrough" : true, "tappedDepth" : 12 * mm, "tapClearance" : 3, "locations" : qUnion([Q0]), "scope" : qUnion([Q1])});
        }
        {
            var Q0;
            Q0=makeQuery(id+"F7.opExtrude","CAP_EDGE",EDGE,{"disambiguationData":[OSD([sQuery(id+"F6.wireOp",EDGE,"E46.top")])],"isStart":false});
            chamfer(context, id + "F15", {"entities" : qUnion([Q0]), "width" : 12 * mm, "tangentPropagation" : true});
        }
        {
            var Q0;
            Q0=makeQuery(id+"F1.opExtrude","CAP_FACE",FACE,{"disambiguationData":[OSD([sQuery(id+"F0.wireOp",EDGE,"E5.0"),sQuery(id+"F0.wireOp",EDGE,"E5.1"),sQuery(id+"F0.wireOp",EDGE,"E5.2"),sQuery(id+"F0.wireOp",EDGE,"E5.3"),sQuery(id+"F0.wireOp",EDGE,"E5.4"),sQuery(id+"F0.wireOp",EDGE,"E5.5"),sQuery(id+"F0.wireOp",EDGE,"E6.1.0.1"),sQuery(id+"F0.wireOp",EDGE,"E6.1.0.2"),sQuery(id+"F0.wireOp",EDGE,"E6.1.0.3"),sQuery(id+"F0.wireOp",EDGE,"E6.1.0.9"),sQuery(id+"F0.wireOp",EDGE,"E6.1.0.11"),sQuery(id+"F0.wireOp",EDGE,"E6.1.0.14"),sQuery(id+"F0.wireOp",EDGE,"E6.2.0.1"),sQuery(id+"F0.wireOp",EDGE,"E6.2.0.2"),sQuery(id+"F0.wireOp",EDGE,"E6.2.0.3"),sQuery(id+"F0.wireOp",EDGE,"E6.2.0.9"),sQuery(id+"F0.wireOp",EDGE,"E6.2.0.11"),sQuery(id+"F0.wireOp",EDGE,"E6.2.0.14"),sQuery(id+"F0.wireOp",EDGE,"E6.3.0.1"),sQuery(id+"F0.wireOp",EDGE,"E6.3.0.2"),sQuery(id+"F0.wireOp",EDGE,"E6.3.0.3"),sQuery(id+"F0.wireOp",EDGE,"E6.3.0.9"),sQuery(id+"F0.wireOp",EDGE,"E6.3.0.11"),sQuery(id+"F0.wireOp",EDGE,"E6.3.0.14"),sQuery(id+"F0.wireOp",EDGE,"E6.4.0.1"),sQuery(id+"F0.wireOp",EDGE,"E6.4.0.2"),sQuery(id+"F0.wireOp",EDGE,"E6.4.0.3"),sQuery(id+"F0.wireOp",EDGE,"E6.4.0.9"),sQuery(id+"F0.wireOp",EDGE,"E6.4.0.11"),sQuery(id+"F0.wireOp",EDGE,"E6.4.0.14"),sQuery(id+"F0.wireOp",EDGE,"E6.5.0.1"),sQuery(id+"F0.wireOp",EDGE,"E6.5.0.2"),sQuery(id+"F0.wireOp",EDGE,"E6.5.0.3"),sQuery(id+"F0.wireOp",EDGE,"E6.5.0.9"),sQuery(id+"F0.wireOp",EDGE,"E6.5.0.11"),sQuery(id+"F0.wireOp",EDGE,"E6.5.0.14"),sQuery(id+"F0.wireOp",EDGE,"E11.bottom"),sQuery(id+"F0.wireOp",EDGE,"E11.top"),sQuery(id+"F0.wireOp",EDGE,"E11.left"),sQuery(id+"F0.wireOp",EDGE,"E11.right"),sQuery(id+"F0.wireOp",EDGE,"E16.filletArc"),sQuery(id+"F0.wireOp",EDGE,"E17.filletArc"),sQuery(id+"F0.wireOp",EDGE,"E18.filletArc"),sQuery(id+"F0.wireOp",EDGE,"E19.filletArc")])],"isStart":false});
            var sketch = newSketch(context, id + "F16", { "sketchPlane" : qUnion([Q0])});
            skArc(sketch, "E59", {"start": v(-56.45, 70.51) * mm, "mid": v(-48.5, 72.56) * mm, "end": v(-46.45, 80.51) * mm});
            skLineSegment(sketch, "E60", {"start": v(18.55, 80.51) * mm, "end": v(18.55, -19.49) * mm, "construction": true});
            skLineSegment(sketch, "E61", {"start": v(-56.45, 30.51) * mm, "end": v(93.55, 30.51) * mm, "construction": true});
            skArc(sketch, "E62.MirrorCS", {"start": v(-56.45, -9.49) * mm, "mid": v(-48.5, -11.53) * mm, "end": v(-46.45, -19.49) * mm});
            skLineSegment(sketch, "E63.MirrorCS", {"start": v(18.55, -19.49) * mm, "end": v(18.55, 80.51) * mm, "construction": true});
            skArc(sketch, "E64.MirrorCS", {"start": v(93.55, -9.49) * mm, "mid": v(85.6, -11.53) * mm, "end": v(83.55, -19.49) * mm});
            skArc(sketch, "E65.MirrorCS", {"start": v(93.55, 70.51) * mm, "mid": v(85.6, 72.56) * mm, "end": v(83.55, 80.51) * mm});
            skSolve(sketch);
        }
        {
            var Q0;
            Q0=makeQuery(id+"F16.imprint","IMPRINT",FACE,{"disambiguationData":[TD([[makeQuery(id+"F16.imprint","IMPRINT",EDGE,{"derivedFrom":sQuery(id+"F16.wireOp",EDGE,"E59")}),1.0]])]});
            var Q1;
            Q1=makeQuery(id+"F16.imprint","IMPRINT",FACE,{"disambiguationData":[TD([[makeQuery(id+"F16.imprint","IMPRINT",EDGE,{"derivedFrom":sQuery(id+"F16.wireOp",EDGE,"E65.MirrorCS")}),-1.0]])]});
            var Q2;
            Q2=makeQuery(id+"F16.imprint","IMPRINT",FACE,{"disambiguationData":[TD([[makeQuery(id+"F16.imprint","IMPRINT",EDGE,{"derivedFrom":sQuery(id+"F16.wireOp",EDGE,"E64.MirrorCS")}),1.0]])]});
            var Q3;
            Q3=makeQuery(id+"F16.imprint","IMPRINT",FACE,{"disambiguationData":[TD([[makeQuery(id+"F16.imprint","IMPRINT",EDGE,{"derivedFrom":sQuery(id+"F16.wireOp",EDGE,"E62.MirrorCS")}),-1.0]])]});
            extrude(context, id + "F17", {"entities" : qUnion([Q0, Q1, Q2, Q3]), "depth" : 15 * mm, "offsetDistance" : 25 * mm});
        }
        {
            var Q0;
            Q0=makeQuery(id+"F17.opExtrude","CAP_EDGE",EDGE,{"disambiguationData":[OSD([sQuery(id+"F16.wireOp",EDGE,"E59")])],"isStart":false});
            var Q1;
            Q1=makeQuery(id+"F17.opExtrude","CAP_EDGE",EDGE,{"disambiguationData":[OSD([sQuery(id+"F16.wireOp",EDGE,"E62.MirrorCS")])],"isStart":false});
            var Q2;
            Q2=makeQuery(id+"F17.opExtrude","CAP_EDGE",EDGE,{"disambiguationData":[OSD([sQuery(id+"F16.wireOp",EDGE,"E65.MirrorCS")])],"isStart":false});
            var Q3;
            Q3=makeQuery(id+"F17.opExtrude","CAP_EDGE",EDGE,{"disambiguationData":[OSD([sQuery(id+"F16.wireOp",EDGE,"E64.MirrorCS")])],"isStart":false});
            chamfer(context, id + "F18", {"entities" : qUnion([Q0, Q1, Q2, Q3]), "width" : 7 * mm, "tangentPropagation" : true});
        }
    });
